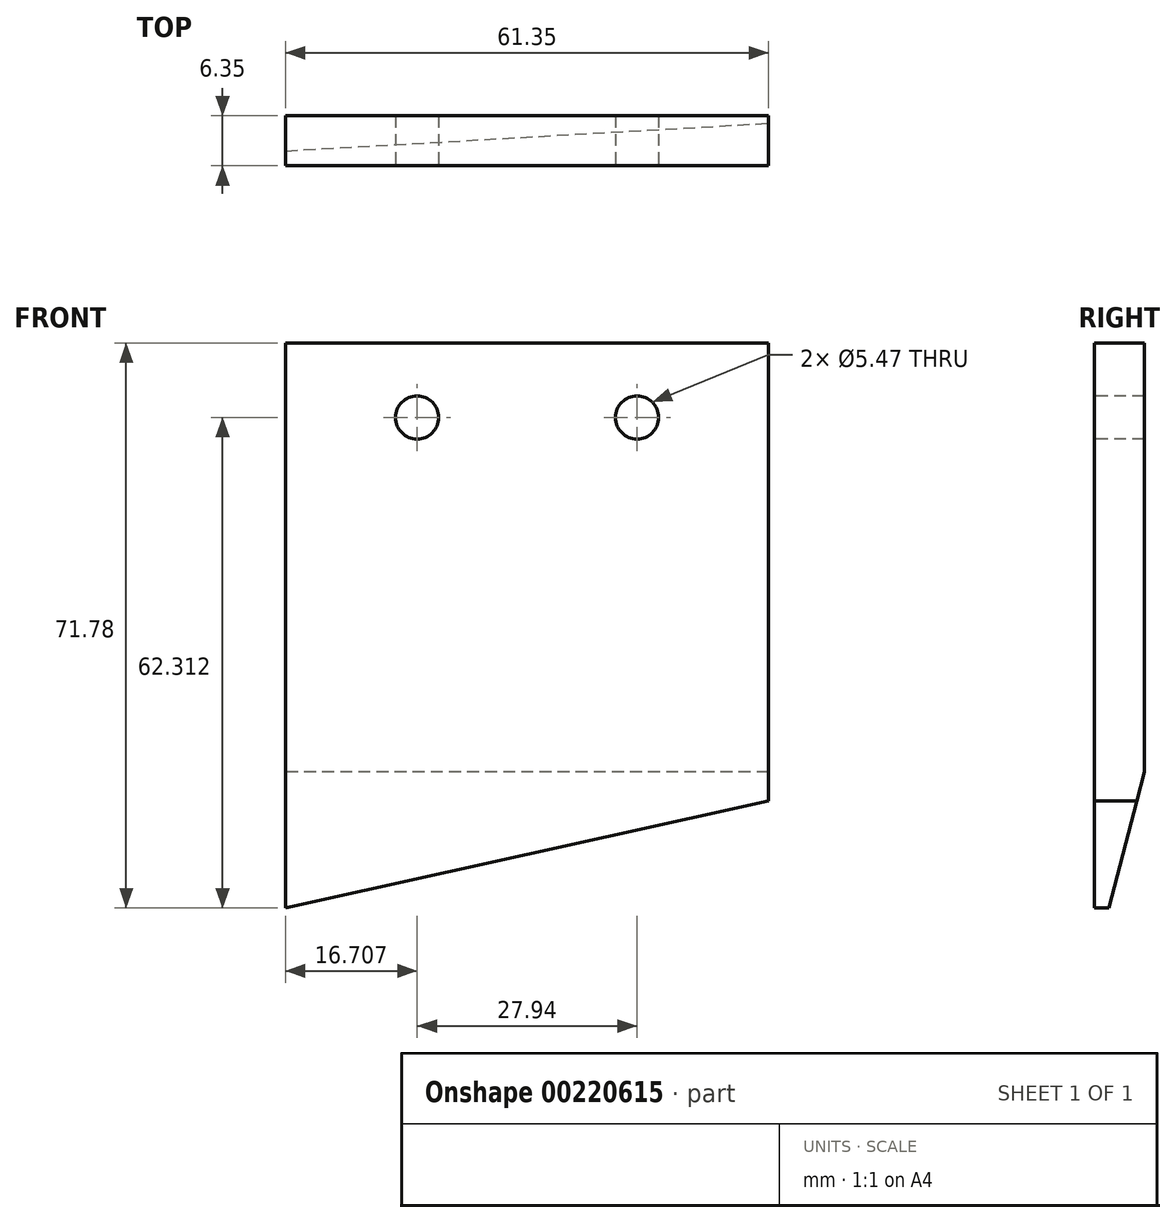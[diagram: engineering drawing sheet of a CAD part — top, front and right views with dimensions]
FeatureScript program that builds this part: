
annotation { "Feature Type Name" : "Feature", "Feature Type Description" : "" }
export const myFeature = defineFeature(function(context is Context, id is Id, definition is map)
    precondition{}
    {
        {
            var Q0;
            Q0=qCreatedBy(makeId("Front.planeOp"),FACE);
            var sketch = newSketch(context, id + "F0", { "sketchPlane" : qUnion([Q0])});
            skLineSegment(sketch, "E0.bottom", {"start": v(0, 0) * mm, "end": v(61.35, 0) * mm});
            skLineSegment(sketch, "E0.left", {"start": v(0, 0) * mm, "end": v(0, -71.78) * mm});
            skLineSegment(sketch, "E1", {"start": v(61.35, 0) * mm, "end": v(61.35, -58.17) * mm});
            skLineSegment(sketch, "E2", {"start": v(61.35, -58.17) * mm, "end": v(0, -71.78) * mm});
            skSolve(sketch);
        }
        {
            var Q0;
            Q0=makeQuery(id+"F0.imprint","IMPRINT",FACE,{"disambiguationData":[TD([[makeQuery(id+"F0.imprint","IMPRINT",EDGE,{"derivedFrom":sQuery(id+"F0.wireOp",EDGE,"E0.bottom")}),-1.0]])]});
            extrude(context, id + "F1", {"entities" : qUnion([Q0]), "depth" : 6.35 * mm});
        }
        {
            var Q0;
            Q0=makeQuery(id+"F1.opExtrude","CAP_FACE",FACE,{"disambiguationData":[OSD([sQuery(id+"F0.wireOp",EDGE,"E0.bottom"),sQuery(id+"F0.wireOp",EDGE,"E0.left"),sQuery(id+"F0.wireOp",EDGE,"E1"),sQuery(id+"F0.wireOp",EDGE,"E2")])],"isStart":false});
            var sketch = newSketch(context, id + "F2", { "sketchPlane" : qUnion([Q0])});
            skCircle(sketch, "E3", {"center": v(16.7, -9.47) * mm, "radius": 2.74 * mm});
            skCircle(sketch, "E4", {"center": v(44.65, -9.47) * mm, "radius": 2.74 * mm});
            skSolve(sketch);
        }
        {
            var Q0;
            Q0=makeQuery(id+"F2.imprint","IMPRINT",FACE,{"disambiguationData":[TD([[makeQuery(id+"F2.imprint","IMPRINT",EDGE,{"derivedFrom":sQuery(id+"F2.wireOp",EDGE,"E4")}),1.0]])]});
            var Q1;
            Q1=makeQuery(id+"F2.imprint","IMPRINT",FACE,{"disambiguationData":[TD([[makeQuery(id+"F2.imprint","IMPRINT",EDGE,{"derivedFrom":sQuery(id+"F2.wireOp",EDGE,"E3")}),1.0]])]});
            extrude(context, id + "F3", {"entities" : qUnion([Q0, Q1]), "operationType" : NewBodyOperationType.REMOVE, "oppositeDirection" : true, "depth" : 6.35 * mm});
        }
        {
            var Q0;
            Q0=makeQuery(id+"F1.opExtrude","SWEPT_FACE",FACE,{"disambiguationData":[OSD([sQuery(id+"F0.wireOp",EDGE,"E0.left")])]});
            var sketch = newSketch(context, id + "F4", { "sketchPlane" : qUnion([Q0])});
            skLineSegment(sketch, "E5", {"start": v(0, -54.5) * mm, "end": v(4.45, -71.78) * mm});
            skLineSegment(sketch, "E6", {"start": v(0, -54.5) * mm, "end": v(0, -71.78) * mm});
            skLineSegment(sketch, "E7", {"start": v(0, -71.78) * mm, "end": v(4.45, -71.78) * mm});
            skSolve(sketch);
        }
        {
            var Q0;
            Q0=makeQuery(id+"F4.imprint","IMPRINT",FACE,{"disambiguationData":[TD([[makeQuery(id+"F4.imprint","IMPRINT",EDGE,{"derivedFrom":sQuery(id+"F4.wireOp",EDGE,"E5")}),-1.0]])]});
            extrude(context, id + "F5", {"entities" : qUnion([Q0]), "operationType" : NewBodyOperationType.REMOVE, "oppositeDirection" : true, "depth" : 63.5 * mm});
        }
    });
